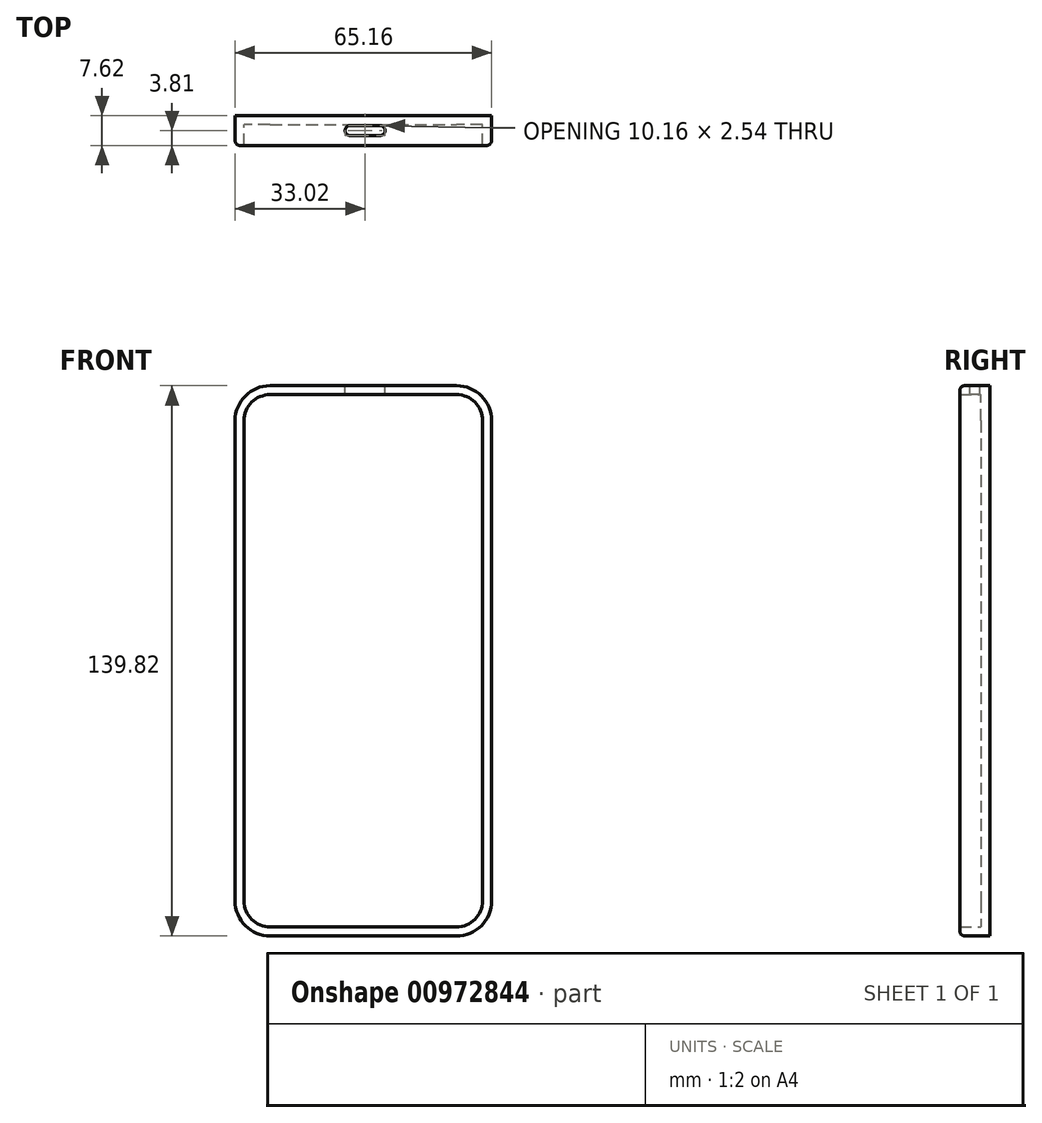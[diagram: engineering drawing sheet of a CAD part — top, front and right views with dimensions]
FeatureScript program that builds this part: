
annotation { "Feature Type Name" : "Feature", "Feature Type Description" : "" }
export const myFeature = defineFeature(function(context is Context, id is Id, definition is map)
    precondition{}
    {
        {
            var Q0;
            Q0=qCreatedBy(makeId("Front.planeOp"),FACE);
            var sketch = newSketch(context, id + "F0", { "sketchPlane" : qUnion([Q0])});
            skLineSegment(sketch, "E0.bottom", {"start": v(-24.13, 63.87) * mm, "end": v(23.25, 63.87) * mm});
            skLineSegment(sketch, "E0.top", {"start": v(-24.13, -75.95) * mm, "end": v(23.25, -75.95) * mm});
            skLineSegment(sketch, "E0.left", {"start": v(-33.02, 54.98) * mm, "end": v(-33.02, -67.06) * mm});
            skLineSegment(sketch, "E0.right", {"start": v(32.14, 54.98) * mm, "end": v(32.14, -67.06) * mm});
            skPoint(sketch, "E1.visualSharp", {"position": v(-33.02, 63.87) * mm});
            skArc(sketch, "E1.filletArc", {"start": v(-24.13, 63.87) * mm, "mid": v(-30.41, 61.27) * mm, "end": v(-33.02, 54.98) * mm});
            skPoint(sketch, "E2.visualSharp", {"position": v(32.14, 63.87) * mm});
            skArc(sketch, "E2.filletArc", {"start": v(32.14, 54.98) * mm, "mid": v(29.54, 61.27) * mm, "end": v(23.25, 63.87) * mm});
            skPoint(sketch, "E3.visualSharp", {"position": v(32.14, -75.95) * mm});
            skArc(sketch, "E3.filletArc", {"start": v(23.25, -75.95) * mm, "mid": v(29.54, -73.35) * mm, "end": v(32.14, -67.06) * mm});
            skPoint(sketch, "E4.visualSharp", {"position": v(-33.02, -75.95) * mm});
            skArc(sketch, "E4.filletArc", {"start": v(-33.02, -67.06) * mm, "mid": v(-30.41, -73.35) * mm, "end": v(-24.13, -75.95) * mm});
            skSolve(sketch);
        }
        {
            var Q0;
            Q0=makeQuery(id+"F0.imprint","IMPRINT",FACE,{"disambiguationData":[TD([[makeQuery(id+"F0.imprint","IMPRINT",EDGE,{"derivedFrom":sQuery(id+"F0.wireOp",EDGE,"E0.bottom")}),-1.0]])]});
            extrude(context, id + "F1", {"entities" : qUnion([Q0]), "depth" : 7.62 * mm, "offsetDistance" : 25.4 * mm});
        }
        {
            var Q0;
            Q0=makeQuery(id+"F1.opExtrude","CAP_FACE",FACE,{"disambiguationData":[OSD([sQuery(id+"F0.wireOp",EDGE,"E0.bottom"),sQuery(id+"F0.wireOp",EDGE,"E0.top"),sQuery(id+"F0.wireOp",EDGE,"E0.left"),sQuery(id+"F0.wireOp",EDGE,"E0.right"),sQuery(id+"F0.wireOp",EDGE,"E1.filletArc"),sQuery(id+"F0.wireOp",EDGE,"E2.filletArc"),sQuery(id+"F0.wireOp",EDGE,"E3.filletArc"),sQuery(id+"F0.wireOp",EDGE,"E4.filletArc")])],"isStart":false});
            var sketch = newSketch(context, id + "F2", { "sketchPlane" : qUnion([Q0])});
            skLineSegment(sketch, "E5", {"start": v(-28.57, 54.98) * mm, "end": v(-28.57, -67.06) * mm});
            skLineSegment(sketch, "E6", {"start": v(-28.57, -67.06) * mm, "end": v(27.7, -67.06) * mm});
            skLineSegment(sketch, "E7", {"start": v(27.7, -67.06) * mm, "end": v(27.7, 54.98) * mm});
            skLineSegment(sketch, "E8", {"start": v(27.7, 54.98) * mm, "end": v(-28.57, 54.98) * mm});
            skSolve(sketch);
        }
        {
            var Q0;
            Q0=makeQuery(id+"F1.opExtrude","CAP_FACE",FACE,{"disambiguationData":[OSD([sQuery(id+"F0.wireOp",EDGE,"E0.bottom"),sQuery(id+"F0.wireOp",EDGE,"E0.top"),sQuery(id+"F0.wireOp",EDGE,"E0.left"),sQuery(id+"F0.wireOp",EDGE,"E0.right"),sQuery(id+"F0.wireOp",EDGE,"E1.filletArc"),sQuery(id+"F0.wireOp",EDGE,"E2.filletArc"),sQuery(id+"F0.wireOp",EDGE,"E3.filletArc"),sQuery(id+"F0.wireOp",EDGE,"E4.filletArc")])],"isStart":false});
            shell(context, id + "F3", {"entities" : qUnion([Q0]), "thickness" : 2.3 * mm});
        }
        {
            var Q0;
            Q0=makeQuery(id+"F1.opExtrude","SWEPT_FACE",FACE,{"disambiguationData":[OSD([sQuery(id+"F0.wireOp",EDGE,"E0.bottom")])]});
            var sketch = newSketch(context, id + "F4", { "sketchPlane" : qUnion([Q0])});
            skLineSegment(sketch, "E9.bottom", {"start": v(0, 0) * mm, "end": v(0, 0) * mm});
            skLineSegment(sketch, "E9.top", {"start": v(0, -7.62) * mm, "end": v(0, -7.62) * mm});
            skPoint(sketch, "E10.visualSharp", {"position": v(0, -2.54) * mm});
            skPoint(sketch, "E11.visualSharp", {"position": v(0, -5.08) * mm});
            skLineSegment(sketch, "E12.bottom", {"start": v(-3.81, -2.54) * mm, "end": v(3.81, -2.54) * mm});
            skLineSegment(sketch, "E12.top", {"start": v(-3.81, -5.08) * mm, "end": v(3.81, -5.08) * mm});
            skLineSegment(sketch, "E12.right", {"start": v(5.08, -3.8) * mm, "end": v(5.08, -3.81) * mm});
            skLineSegment(sketch, "E13", {"start": v(-5.08, -3.81) * mm, "end": v(-5.08, -3.8) * mm});
            skPoint(sketch, "E14.visualSharp", {"position": v(-5.08, -2.54) * mm});
            skArc(sketch, "E14.filletArc", {"start": v(-3.81, -2.54) * mm, "mid": v(-4.7, -2.91) * mm, "end": v(-5.08, -3.8) * mm});
            skPoint(sketch, "E15.visualSharp", {"position": v(-5.08, -5.08) * mm});
            skArc(sketch, "E15.filletArc", {"start": v(-5.08, -3.81) * mm, "mid": v(-4.7, -4.7) * mm, "end": v(-3.81, -5.08) * mm});
            skPoint(sketch, "E16.visualSharp", {"position": v(5.08, -2.54) * mm});
            skArc(sketch, "E16.filletArc", {"start": v(5.08, -3.8) * mm, "mid": v(4.7, -2.91) * mm, "end": v(3.81, -2.54) * mm});
            skPoint(sketch, "E17.visualSharp", {"position": v(5.08, -5.08) * mm});
            skArc(sketch, "E17.filletArc", {"start": v(3.81, -5.08) * mm, "mid": v(4.7, -4.7) * mm, "end": v(5.08, -3.81) * mm});
            skSolve(sketch);
        }
        {
            var Q0;
            Q0 = qSketchRegion(id + "F4", true);
            extrude(context, id + "F5", {"entities" : qUnion([Q0]), "operationType" : NewBodyOperationType.REMOVE, "oppositeDirection" : true, "depth" : 15.57 * mm, "offsetDistance" : 25.4 * mm});
        }
        {
            var Q0;
            Q0=makeQuery(id+"F1.opExtrude","CAP_EDGE",EDGE,{"disambiguationData":[OSD([sQuery(id+"F0.wireOp",EDGE,"E0.top")])],"isStart":false});
            var Q1;
            Q1=makeQuery(id+"F1.opExtrude","CAP_EDGE",EDGE,{"disambiguationData":[OSD([sQuery(id+"F0.wireOp",EDGE,"E3.filletArc")])],"isStart":false});
            var Q2;
            Q2=makeQuery(id+"F1.opExtrude","CAP_EDGE",EDGE,{"disambiguationData":[OSD([sQuery(id+"F0.wireOp",EDGE,"E0.right")])],"isStart":false});
            var Q3;
            Q3=makeQuery(id+"F1.opExtrude","CAP_EDGE",EDGE,{"disambiguationData":[OSD([sQuery(id+"F0.wireOp",EDGE,"E2.filletArc")])],"isStart":false});
            var Q4;
            Q4=makeQuery(id+"F1.opExtrude","CAP_EDGE",EDGE,{"disambiguationData":[OSD([sQuery(id+"F0.wireOp",EDGE,"E0.bottom")])],"isStart":false});
            var Q5;
            Q5=makeQuery(id+"F1.opExtrude","CAP_EDGE",EDGE,{"disambiguationData":[OSD([sQuery(id+"F0.wireOp",EDGE,"E4.filletArc")])],"isStart":false});
            var Q6;
            Q6=makeQuery(id+"F1.opExtrude","CAP_EDGE",EDGE,{"disambiguationData":[OSD([sQuery(id+"F0.wireOp",EDGE,"E0.left")])],"isStart":false});
            fillet(context, id + "F6", {"entities" : qUnion([Q0, Q1, Q2, Q3, Q4, Q5, Q6]), "radius" : 1.27 * mm, "tangentPropagation" : true, "allowEdgeOverflow" : false});
        }
    });
